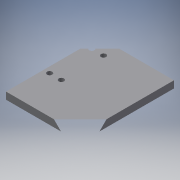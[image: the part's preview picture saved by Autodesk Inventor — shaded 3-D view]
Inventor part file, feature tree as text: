
AUTODESK INVENTOR PART (.ipt)
format: ipt  version: 2016 (Build 200138000, 138)  size: 122,368 bytes
history: native  units: mm
features: reference x4, extrude x3, sketch x3, fillet x1
ambient origin geometry x8: Origin, YZ Plane, XZ Plane, XY Plane, X Axis, Y Axis, Z Axis, Center Point
bodies: Solid1 (feature_tree)
feature tree (11):
  extrude  "Extrusion1"  Depth=95.0mm
  extrude  "Extrusion3"  Depth=7.0mm
  fillet  "Fillet1"  Radius=35.0mm
  extrude  "Extrusion4"  Depth=3.0mm TaperAngle=0.0deg
  sketch  "Sketch1"  dims[d0=120.0mm d1=95.0mm]
  sketch  "Sketch3"  dims[d2=6.0mm d3=0.0mm d9=7.0mm d10=35.0mm]
  sketch  "Sketch4"  dims[d11=75.0mm d12=3.0mm d13=0.0mm d14=7.0mm d15=10.0mm d16=0.0mm]
  reference  "Reference1"
  reference  "Reference2"
  reference  "Reference3"
  reference  "Reference4"
